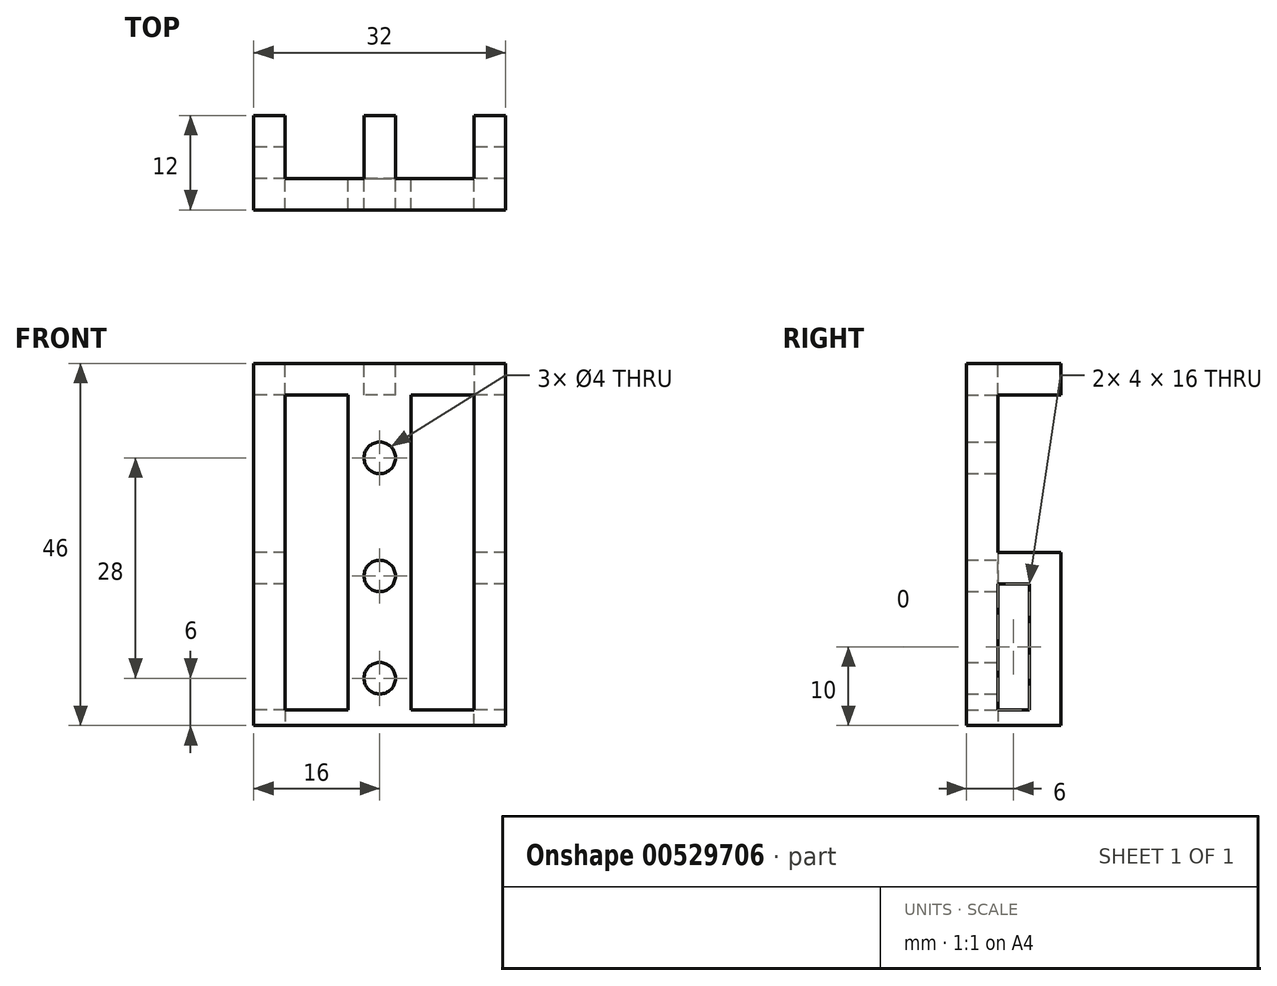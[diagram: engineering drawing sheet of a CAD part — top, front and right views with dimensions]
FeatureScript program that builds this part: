
annotation { "Feature Type Name" : "Feature", "Feature Type Description" : "" }
export const myFeature = defineFeature(function(context is Context, id is Id, definition is map)
    precondition{}
    {
        {
            var Q0;
            Q0=qCreatedBy(makeId("Front.planeOp"),FACE);
            var sketch = newSketch(context, id + "F0", { "sketchPlane" : qUnion([Q0])});
            skLineSegment(sketch, "E0.bottom", {"start": v(-16, 0) * mm, "end": v(16, 0) * mm});
            skLineSegment(sketch, "E0.top", {"start": v(-16, -46) * mm, "end": v(16, -46) * mm});
            skLineSegment(sketch, "E0.left", {"start": v(-16, -46) * mm, "end": v(-16, 0) * mm});
            skLineSegment(sketch, "E0.right", {"start": v(16, -46) * mm, "end": v(16, 0) * mm});
            skLineSegment(sketch, "E1.bottom", {"start": v(4, -4) * mm, "end": v(12, -4) * mm});
            skLineSegment(sketch, "E1.top", {"start": v(4, -44) * mm, "end": v(12, -44) * mm});
            skLineSegment(sketch, "E1.left", {"start": v(4, -4) * mm, "end": v(4, -44) * mm});
            skLineSegment(sketch, "E1.right", {"start": v(12, -4) * mm, "end": v(12, -44) * mm});
            skCircle(sketch, "E2", {"center": v(0, -12) * mm, "radius": 2 * mm});
            skCircle(sketch, "E3", {"center": v(0, -27) * mm, "radius": 2 * mm});
            skLineSegment(sketch, "E4.MirrorCS", {"start": v(-4, -4) * mm, "end": v(-12, -4) * mm});
            skLineSegment(sketch, "E5.MirrorCS", {"start": v(-4, -44) * mm, "end": v(-12, -44) * mm});
            skLineSegment(sketch, "E6.MirrorCS", {"start": v(-12, -4) * mm, "end": v(-12, -44) * mm});
            skLineSegment(sketch, "E7.MirrorCS", {"start": v(-4, -4) * mm, "end": v(-4, -44) * mm});
            skCircle(sketch, "E8", {"center": v(0, -40) * mm, "radius": 2 * mm});
            skSolve(sketch);
        }
        {
            var Q0;
            Q0 = qSketchRegion(id + "F0", true);
            extrude(context, id + "F1", {"entities" : qUnion([Q0]), "depth" : 4 * mm, "offsetDistance" : 25 * mm});
        }
        {
            var Q0;
            Q0=makeQuery(id+"F1.opExtrude","CAP_FACE",FACE,{"disambiguationData":[OSD([sQuery(id+"F0.wireOp",EDGE,"E0.bottom"),sQuery(id+"F0.wireOp",EDGE,"E0.top"),sQuery(id+"F0.wireOp",EDGE,"E0.left"),sQuery(id+"F0.wireOp",EDGE,"E0.right"),sQuery(id+"F0.wireOp",EDGE,"E1.bottom"),sQuery(id+"F0.wireOp",EDGE,"E1.top"),sQuery(id+"F0.wireOp",EDGE,"E1.left"),sQuery(id+"F0.wireOp",EDGE,"E1.right"),sQuery(id+"F0.wireOp",EDGE,"E2"),sQuery(id+"F0.wireOp",EDGE,"E3"),sQuery(id+"F0.wireOp",EDGE,"E4.MirrorCS"),sQuery(id+"F0.wireOp",EDGE,"E5.MirrorCS"),sQuery(id+"F0.wireOp",EDGE,"E6.MirrorCS"),sQuery(id+"F0.wireOp",EDGE,"E7.MirrorCS")])],"isStart":true});
            var sketch = newSketch(context, id + "F2", { "sketchPlane" : qUnion([Q0])});
            skLineSegment(sketch, "E9.bottom", {"start": v(-16, -46) * mm, "end": v(-12, -46) * mm});
            skLineSegment(sketch, "E9.top", {"start": v(-16, -44) * mm, "end": v(-12, -44) * mm});
            skLineSegment(sketch, "E9.left", {"start": v(-16, -46) * mm, "end": v(-16, -44) * mm});
            skLineSegment(sketch, "E9.right", {"start": v(-12, -46) * mm, "end": v(-12, -44) * mm});
            skLineSegment(sketch, "E10.bottom", {"start": v(12, -44) * mm, "end": v(16, -44) * mm});
            skLineSegment(sketch, "E10.top", {"start": v(12, -46) * mm, "end": v(16, -46) * mm});
            skLineSegment(sketch, "E10.left", {"start": v(12, -44) * mm, "end": v(12, -46) * mm});
            skLineSegment(sketch, "E10.right", {"start": v(16, -44) * mm, "end": v(16, -46) * mm});
            skLineSegment(sketch, "E11.bottom", {"start": v(-16, 0) * mm, "end": v(-12, 0) * mm});
            skLineSegment(sketch, "E11.top", {"start": v(-16, -4) * mm, "end": v(-12, -4) * mm});
            skLineSegment(sketch, "E11.left", {"start": v(-16, 0) * mm, "end": v(-16, -4) * mm});
            skLineSegment(sketch, "E11.right", {"start": v(-12, 0) * mm, "end": v(-12, -4) * mm});
            skLineSegment(sketch, "E12.bottom", {"start": v(12, -4) * mm, "end": v(16, -4) * mm});
            skLineSegment(sketch, "E12.top", {"start": v(12, 0) * mm, "end": v(16, 0) * mm});
            skLineSegment(sketch, "E12.left", {"start": v(12, -4) * mm, "end": v(12, 0) * mm});
            skLineSegment(sketch, "E12.right", {"start": v(16, -4) * mm, "end": v(16, 0) * mm});
            skLineSegment(sketch, "E13.bottom", {"start": v(-2, -4) * mm, "end": v(2, -4) * mm});
            skLineSegment(sketch, "E13.top", {"start": v(-2, 0) * mm, "end": v(2, 0) * mm});
            skLineSegment(sketch, "E13.left", {"start": v(-2, -4) * mm, "end": v(-2, 0) * mm});
            skLineSegment(sketch, "E13.right", {"start": v(2, -4) * mm, "end": v(2, 0) * mm});
            skLineSegment(sketch, "E14.bottom", {"start": v(-16, -24) * mm, "end": v(-12, -24) * mm});
            skLineSegment(sketch, "E14.top", {"start": v(-16, -28) * mm, "end": v(-12, -28) * mm});
            skLineSegment(sketch, "E14.left", {"start": v(-16, -24) * mm, "end": v(-16, -28) * mm});
            skLineSegment(sketch, "E14.right", {"start": v(-12, -24) * mm, "end": v(-12, -28) * mm});
            skLineSegment(sketch, "E15.bottom", {"start": v(12, -24) * mm, "end": v(16, -24) * mm});
            skLineSegment(sketch, "E15.top", {"start": v(12, -28) * mm, "end": v(16, -28) * mm});
            skLineSegment(sketch, "E15.left", {"start": v(12, -24) * mm, "end": v(12, -28) * mm});
            skLineSegment(sketch, "E15.right", {"start": v(16, -24) * mm, "end": v(16, -28) * mm});
            skSolve(sketch);
        }
        {
            var Q0;
            Q0 = qSketchRegion(id + "F2", true);
            extrude(context, id + "F3", {"entities" : qUnion([Q0]), "operationType" : NewBodyOperationType.ADD, "depth" : 8 * mm, "offsetDistance" : 25 * mm});
        }
        {
            var Q0;
            Q0=makeQuery(id+"F3.opExtrude","CAP_FACE",FACE,{"disambiguationData":[OSD([sQuery(id+"F2.wireOp",EDGE,"E14.bottom"),sQuery(id+"F2.wireOp",EDGE,"E14.top"),sQuery(id+"F2.wireOp",EDGE,"E14.left"),sQuery(id+"F2.wireOp",EDGE,"E14.right")])],"isStart":false});
            var sketch = newSketch(context, id + "F4", { "sketchPlane" : qUnion([Q0])});
            skLineSegment(sketch, "E16.bottom", {"start": v(-16, -24) * mm, "end": v(-12, -24) * mm});
            skLineSegment(sketch, "E16.top", {"start": v(-16, -46) * mm, "end": v(-12, -46) * mm});
            skLineSegment(sketch, "E16.left", {"start": v(-16, -24) * mm, "end": v(-16, -46) * mm});
            skLineSegment(sketch, "E16.right", {"start": v(-12, -24) * mm, "end": v(-12, -46) * mm});
            skLineSegment(sketch, "E17.bottom", {"start": v(12, -24) * mm, "end": v(16, -24) * mm});
            skLineSegment(sketch, "E17.top", {"start": v(12, -46) * mm, "end": v(16, -46) * mm});
            skLineSegment(sketch, "E17.left", {"start": v(12, -24) * mm, "end": v(12, -46) * mm});
            skLineSegment(sketch, "E17.right", {"start": v(16, -24) * mm, "end": v(16, -46) * mm});
            skSolve(sketch);
        }
        {
            var Q0;
            Q0 = qSketchRegion(id + "F4", true);
            extrude(context, id + "F5", {"entities" : qUnion([Q0]), "operationType" : NewBodyOperationType.ADD, "oppositeDirection" : true, "depth" : 4 * mm, "offsetDistance" : 25 * mm});
        }
    });
